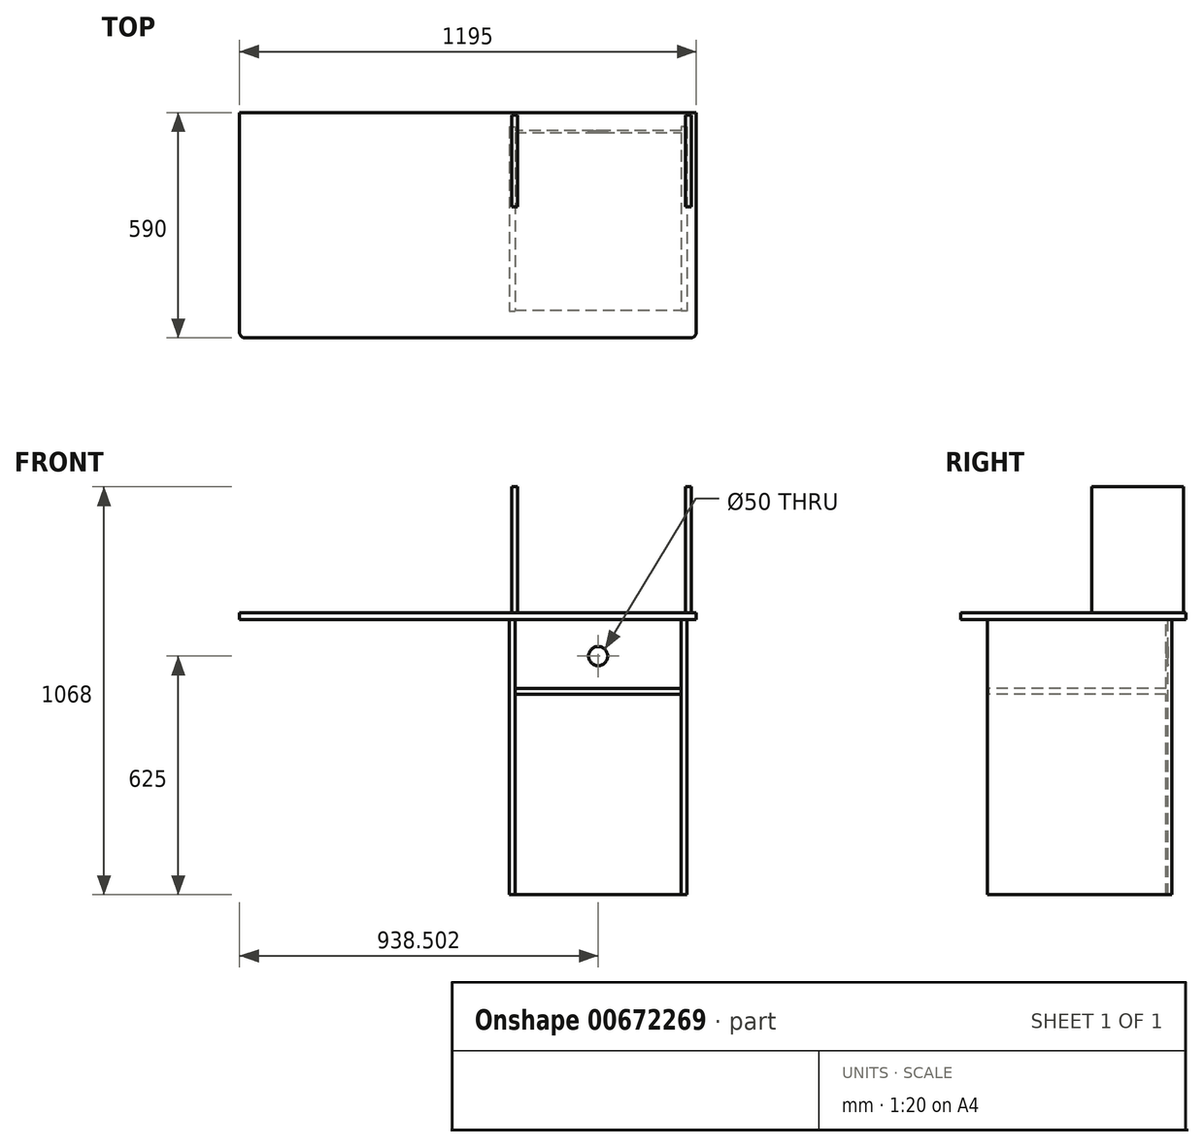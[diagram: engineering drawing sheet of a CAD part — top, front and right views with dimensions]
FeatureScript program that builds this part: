
annotation { "Feature Type Name" : "Feature", "Feature Type Description" : "" }
export const myFeature = defineFeature(function(context is Context, id is Id, definition is map)
    precondition{}
    {
        {
            var Q0;
            Q0=qCreatedBy(makeId("Top.planeOp"),FACE);
            var sketch = newSketch(context, id + "F0", { "sketchPlane" : qUnion([Q0])});
            skLineSegment(sketch, "E0", {"start": v(-44.39, 448.75) * mm, "end": v(-44.39, -16.25) * mm});
            skLineSegment(sketch, "E1", {"start": v(-44.39, -16.25) * mm, "end": v(390.61, -16.25) * mm});
            skLineSegment(sketch, "E2", {"start": v(-44.39, 448.75) * mm, "end": v(390.61, 448.75) * mm});
            skLineSegment(sketch, "E3", {"start": v(390.61, 448.75) * mm, "end": v(390.61, -16.25) * mm});
            skSolve(sketch);
        }
        {
            var Q0;
            Q0 = qSketchRegion(id + "F0", true);
            extrude(context, id + "F1", {"entities" : qUnion([Q0]), "depth" : 15 * mm, "offsetDistance" : 25 * mm});
        }
        {
            var Q0;
            Q0=makeQuery(id+"F1.opExtrude","SWEPT_FACE",FACE,{"disambiguationData":[OSD([sQuery(id+"F0.wireOp",EDGE,"E1")])]});
            var sketch = newSketch(context, id + "F2", { "sketchPlane" : qUnion([Q0])});
            skLineSegment(sketch, "E4", {"start": v(-59.39, 0) * mm, "end": v(-59.39, -525) * mm});
            skLineSegment(sketch, "E5", {"start": v(-59.39, 0) * mm, "end": v(-59.39, 195) * mm});
            skLineSegment(sketch, "E6", {"start": v(-59.39, 195) * mm, "end": v(-44.39, 195) * mm});
            skLineSegment(sketch, "E7", {"start": v(-44.39, 195) * mm, "end": v(-44.39, -525) * mm});
            skLineSegment(sketch, "E8", {"start": v(-59.39, -525) * mm, "end": v(-44.39, -525) * mm});
            skSolve(sketch);
        }
        {
            var Q0;
            Q0 = qSketchRegion(id + "F2", true);
            extrude(context, id + "F3", {"entities" : qUnion([Q0]), "operationType" : NewBodyOperationType.ADD, "oppositeDirection" : true, "depth" : 480 * mm, "offsetDistance" : 25 * mm});
        }
        {
            var Q0;
            Q0 = qSketchRegion(id + "F2", true);
            extrude(context, id + "F4", {"entities" : qUnion([Q0]), "operationType" : NewBodyOperationType.ADD, "depth" : 3 * mm, "offsetDistance" : 25 * mm});
        }
        {
            var Q0;
            Q0=makeQuery(id+"F4.opExtrude","CAP_FACE",FACE,{"disambiguationData":[OSD([sQuery(id+"F2.wireOp",EDGE,"E4"),sQuery(id+"F2.wireOp",EDGE,"E5"),sQuery(id+"F2.wireOp",EDGE,"E6"),sQuery(id+"F2.wireOp",EDGE,"E7"),sQuery(id+"F2.wireOp",EDGE,"E8")])],"isStart":false});
            var sketch = newSketch(context, id + "F5", { "sketchPlane" : qUnion([Q0])});
            skLineSegment(sketch, "E9", {"start": v(405.61, 195) * mm, "end": v(405.61, -525) * mm});
            skLineSegment(sketch, "E10", {"start": v(405.61, -525) * mm, "end": v(390.61, -525) * mm});
            skLineSegment(sketch, "E11", {"start": v(390.61, -525) * mm, "end": v(390.61, 195) * mm});
            skLineSegment(sketch, "E12", {"start": v(390.61, 195) * mm, "end": v(405.61, 195) * mm});
            skSolve(sketch);
        }
        {
            var Q0;
            Q0 = qSketchRegion(id + "F5", true);
            extrude(context, id + "F6", {"entities" : qUnion([Q0]), "operationType" : NewBodyOperationType.ADD, "oppositeDirection" : true, "depth" : 483 * mm, "offsetDistance" : 25 * mm});
        }
        {
            var Q0;
            Q0=makeQuery(id+"F1.opExtrude","SWEPT_FACE",FACE,{"disambiguationData":[OSD([sQuery(id+"F0.wireOp",EDGE,"E2")])]});
            var sketch = newSketch(context, id + "F7", { "sketchPlane" : qUnion([Q0])});
            skLineSegment(sketch, "E13", {"start": v(-390.61, 15) * mm, "end": v(-390.61, 195) * mm});
            skLineSegment(sketch, "E14", {"start": v(-390.61, 15) * mm, "end": v(-390.61, -525) * mm});
            skLineSegment(sketch, "E15", {"start": v(-390.61, -525) * mm, "end": v(44.39, -525) * mm});
            skLineSegment(sketch, "E16", {"start": v(44.39, -525) * mm, "end": v(44.39, 195) * mm});
            skLineSegment(sketch, "E17", {"start": v(44.39, 195) * mm, "end": v(-390.61, 195) * mm});
            skSolve(sketch);
        }
        {
            var Q0;
            Q0 = qSketchRegion(id + "F7", true);
            extrude(context, id + "F8", {"entities" : qUnion([Q0]), "operationType" : NewBodyOperationType.ADD, "depth" : 5 * mm, "offsetDistance" : 25 * mm});
        }
        {
            var Q0;
            Q0=makeQuery(id+"F8.opExtrude","CAP_FACE",FACE,{"disambiguationData":[OSD([sQuery(id+"F7.wireOp",EDGE,"E13"),sQuery(id+"F7.wireOp",EDGE,"E14"),sQuery(id+"F7.wireOp",EDGE,"E15"),sQuery(id+"F7.wireOp",EDGE,"E16"),sQuery(id+"F7.wireOp",EDGE,"E17")])],"isStart":false});
            var sketch = newSketch(context, id + "F9", { "sketchPlane" : qUnion([Q0])});
            skCircle(sketch, "E18", {"center": v(-173.11, 100) * mm, "radius": 25 * mm});
            skSolve(sketch);
        }
        {
            var Q0;
            Q0 = qSketchRegion(id + "F9", true);
            extrude(context, id + "F10", {"entities" : qUnion([Q0]), "operationType" : NewBodyOperationType.REMOVE, "oppositeDirection" : true, "depth" : 5 * mm, "offsetDistance" : 25 * mm});
        }
        {
            var Q0;
            {var subQ0=sQuery(id+"F2.wireOp",EDGE,"E6");Q0=makeQuery(id+"F8.boolean.opBoolean","MERGE",FACE,{"derivedFrom":[makeQuery(id+"F4.boolean.opBoolean","MERGE",FACE,{"derivedFrom":[makeQuery(id+"F3.opExtrude","SWEPT_FACE",FACE,{"disambiguationData":[OSD([subQ0])]}),makeQuery(id+"F4.opExtrude","SWEPT_FACE",FACE,{"disambiguationData":[OSD([subQ0])]})]}),makeQuery(id+"F6.opExtrude","SWEPT_FACE",FACE,{"disambiguationData":[OSD([sQuery(id+"F5.wireOp",EDGE,"E12")])]}),makeQuery(id+"F8.opExtrude","SWEPT_FACE",FACE,{"disambiguationData":[OSD([sQuery(id+"F7.wireOp",EDGE,"E17")])]})]});}
            var sketch = newSketch(context, id + "F11", { "sketchPlane" : qUnion([Q0])});
            skLineSegment(sketch, "E19", {"start": v(414.61, -89.25) * mm, "end": v(-750.39, -89.25) * mm});
            skLineSegment(sketch, "E20", {"start": v(-765.39, -74.25) * mm, "end": v(-765.39, 500.75) * mm});
            skLineSegment(sketch, "E21", {"start": v(-765.39, 500.75) * mm, "end": v(429.61, 500.75) * mm});
            skLineSegment(sketch, "E22", {"start": v(429.61, 500.75) * mm, "end": v(429.61, -74.25) * mm});
            skPoint(sketch, "E23.visualSharp", {"position": v(429.61, -89.25) * mm});
            skArc(sketch, "E23.filletArc", {"start": v(414.61, -89.25) * mm, "mid": v(425.22, -84.86) * mm, "end": v(429.61, -74.25) * mm});
            skPoint(sketch, "E24.visualSharp", {"position": v(-765.39, -89.25) * mm});
            skArc(sketch, "E24.filletArc", {"start": v(-765.39, -74.25) * mm, "mid": v(-761, -84.86) * mm, "end": v(-750.39, -89.25) * mm});
            skSolve(sketch);
        }
        {
            var Q0;
            Q0 = qSketchRegion(id + "F11", true);
            extrude(context, id + "F12", {"entities" : qUnion([Q0]), "operationType" : NewBodyOperationType.ADD, "depth" : 18 * mm, "offsetDistance" : 25 * mm});
        }
        {
            var Q0;
            Q0=makeQuery(id+"F12.opExtrude","CAP_FACE",FACE,{"disambiguationData":[OSD([sQuery(id+"F11.wireOp",EDGE,"E19"),sQuery(id+"F11.wireOp",EDGE,"E20"),sQuery(id+"F11.wireOp",EDGE,"E21"),sQuery(id+"F11.wireOp",EDGE,"E22"),sQuery(id+"F11.wireOp",EDGE,"E23.filletArc"),sQuery(id+"F11.wireOp",EDGE,"E24.filletArc")])],"isStart":false});
            var sketch = newSketch(context, id + "F13", { "sketchPlane" : qUnion([Q0])});
            skLineSegment(sketch, "E25", {"start": v(416.61, 493.75) * mm, "end": v(401.61, 493.75) * mm});
            skLineSegment(sketch, "E26", {"start": v(416.61, 493.75) * mm, "end": v(416.61, 253.75) * mm});
            skLineSegment(sketch, "E27", {"start": v(416.61, 253.75) * mm, "end": v(401.61, 253.75) * mm});
            skLineSegment(sketch, "E28", {"start": v(401.61, 253.75) * mm, "end": v(401.61, 493.75) * mm});
            skSolve(sketch);
        }
        {
            var Q0;
            Q0 = qSketchRegion(id + "F13", true);
            extrude(context, id + "F14", {"entities" : qUnion([Q0]), "operationType" : NewBodyOperationType.ADD, "depth" : 330 * mm, "offsetDistance" : 25 * mm});
        }
        {
            var Q0;
            Q0=makeQuery(id+"F12.opExtrude","CAP_FACE",FACE,{"disambiguationData":[OSD([sQuery(id+"F11.wireOp",EDGE,"E19"),sQuery(id+"F11.wireOp",EDGE,"E20"),sQuery(id+"F11.wireOp",EDGE,"E21"),sQuery(id+"F11.wireOp",EDGE,"E22"),sQuery(id+"F11.wireOp",EDGE,"E23.filletArc"),sQuery(id+"F11.wireOp",EDGE,"E24.filletArc")])],"isStart":false});
            var sketch = newSketch(context, id + "F15", { "sketchPlane" : qUnion([Q0])});
            skLineSegment(sketch, "E29", {"start": v(-38.39, 253.75) * mm, "end": v(-53.39, 253.75) * mm});
            skLineSegment(sketch, "E30", {"start": v(-53.39, 253.75) * mm, "end": v(-53.39, 493.75) * mm});
            skLineSegment(sketch, "E31", {"start": v(-53.39, 493.75) * mm, "end": v(-38.39, 493.75) * mm});
            skLineSegment(sketch, "E32", {"start": v(-38.39, 493.75) * mm, "end": v(-38.39, 253.75) * mm});
            skSolve(sketch);
        }
        {
            var Q0;
            Q0 = qSketchRegion(id + "F15", true);
            extrude(context, id + "F16", {"entities" : qUnion([Q0]), "operationType" : NewBodyOperationType.ADD, "depth" : 330 * mm, "offsetDistance" : 25 * mm});
        }
    });
